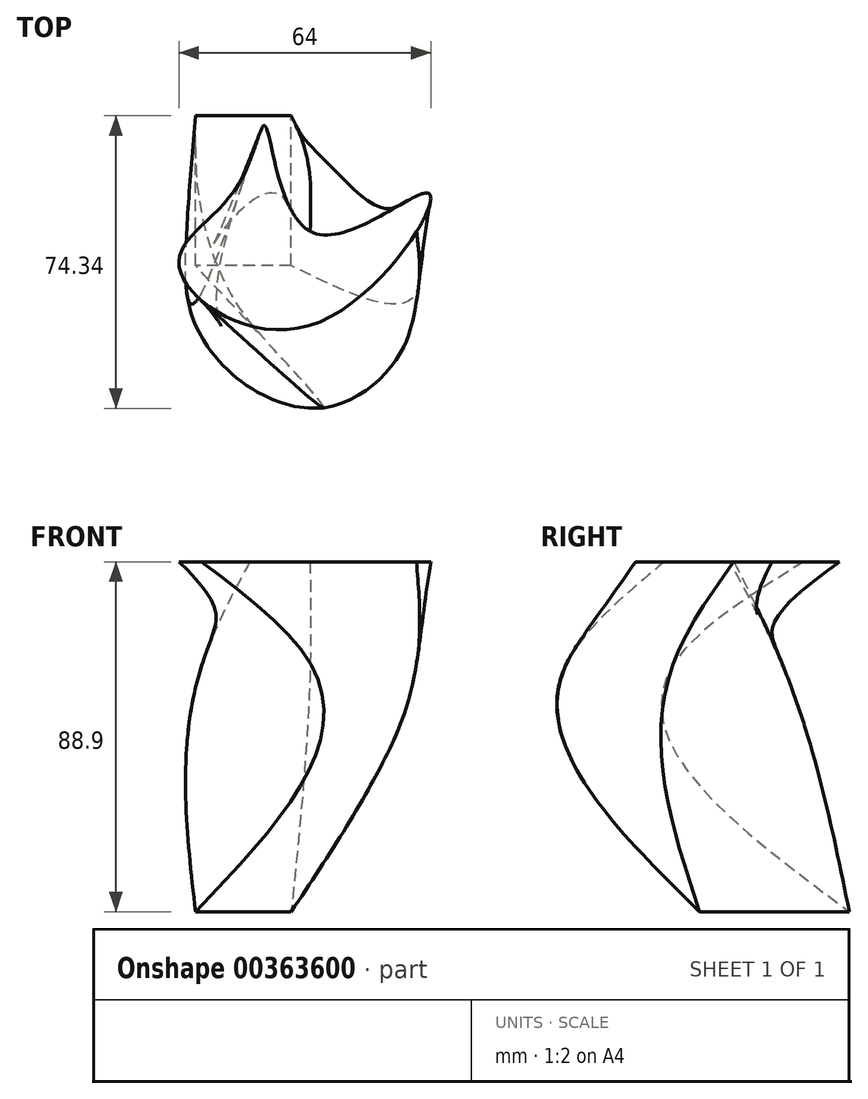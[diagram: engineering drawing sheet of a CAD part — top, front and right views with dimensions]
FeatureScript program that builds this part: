
annotation { "Feature Type Name" : "Feature", "Feature Type Description" : "" }
export const myFeature = defineFeature(function(context is Context, id is Id, definition is map)
    precondition{}
    {
        {
            var Q0;
            Q0=qCreatedBy(makeId("Top.planeOp"),FACE);
            var sketch = newSketch(context, id + "F0", { "sketchPlane" : qUnion([Q0])});
            skLineSegment(sketch, "E0.bottom", {"start": v(0, 0) * mm, "end": v(-24.33, 0) * mm});
            skLineSegment(sketch, "E0.top", {"start": v(0, 38.07) * mm, "end": v(-24.33, 38.07) * mm});
            skLineSegment(sketch, "E0.left", {"start": v(0, 0) * mm, "end": v(0, 38.07) * mm});
            skLineSegment(sketch, "E0.right", {"start": v(-24.33, 0) * mm, "end": v(-24.33, 38.07) * mm});
            skSolve(sketch);
        }
        {
            var Q0;
            Q0=qCreatedBy(makeId("Top.planeOp"),FACE);
            cPlane(context, id + "F1", {"entities" : qUnion([Q0]), "cplaneType" : CPlaneType.OFFSET, "offset" : 63.5 * mm, "width" : 152.4 * mm, "height" : 152.4 * mm});
        }
        {
            var Q0;
            Q0=qCreatedBy(id+"F1.planeOp",FACE);
            var sketch = newSketch(context, id + "F2", { "sketchPlane" : qUnion([Q0])});
            skCircle(sketch, "E1", {"center": v(4.74, -6.36) * mm, "radius": 27.17 * mm});
            skSolve(sketch);
        }
        {
            var Q0;
            Q0=qCreatedBy(id+"F1.planeOp",FACE);
            cPlane(context, id + "F3", {"entities" : qUnion([Q0]), "cplaneType" : CPlaneType.OFFSET, "offset" : 25.4 * mm, "width" : 152.4 * mm, "height" : 152.4 * mm});
        }
        {
            var Q0;
            Q0=qCreatedBy(id+"F3.planeOp",FACE);
            var sketch = newSketch(context, id + "F4", { "sketchPlane" : qUnion([Q0])});
            skFitSpline(sketch, "E2", {"points": [v(-13.61, 20.25) * mm, v(-28.5, 0) * mm, v(5.08, -15.1) * mm, v(34.9, 18.36) * mm, v(5.67, 8.31) * mm, v(-6.57, 35.43) * mm, v(-13.61, 20.25) * mm]});
            skSolve(sketch);
        }
        {
            var Q0;
            Q0=makeQuery(id+"F4.imprint","IMPRINT",FACE,{"disambiguationData":[TD([[makeQuery(id+"F4.imprint","IMPRINT",EDGE,{"derivedFrom":sQuery(id+"F4.wireOp",EDGE,"E2")}),1.0]])]});
            var Q1;
            Q1=makeQuery(id+"F2.imprint","IMPRINT",FACE,{"disambiguationData":[TD([[makeQuery(id+"F2.imprint","IMPRINT",EDGE,{"derivedFrom":sQuery(id+"F2.wireOp",EDGE,"E1")}),1.0]])]});
            var Q2;
            Q2=makeQuery(id+"F0.imprint","IMPRINT",FACE,{"disambiguationData":[TD([[makeQuery(id+"F0.imprint","IMPRINT",EDGE,{"derivedFrom":sQuery(id+"F0.wireOp",EDGE,"E0.bottom")}),-1.0]])]});
            loft(context, id + "F5", {"sheetProfilesArray" : [{ "sheetProfileEntities" : qUnion([Q0]) }, { "sheetProfileEntities" : qUnion([Q1]) }, { "sheetProfileEntities" : qUnion([Q2]) }]});
        }
    });
